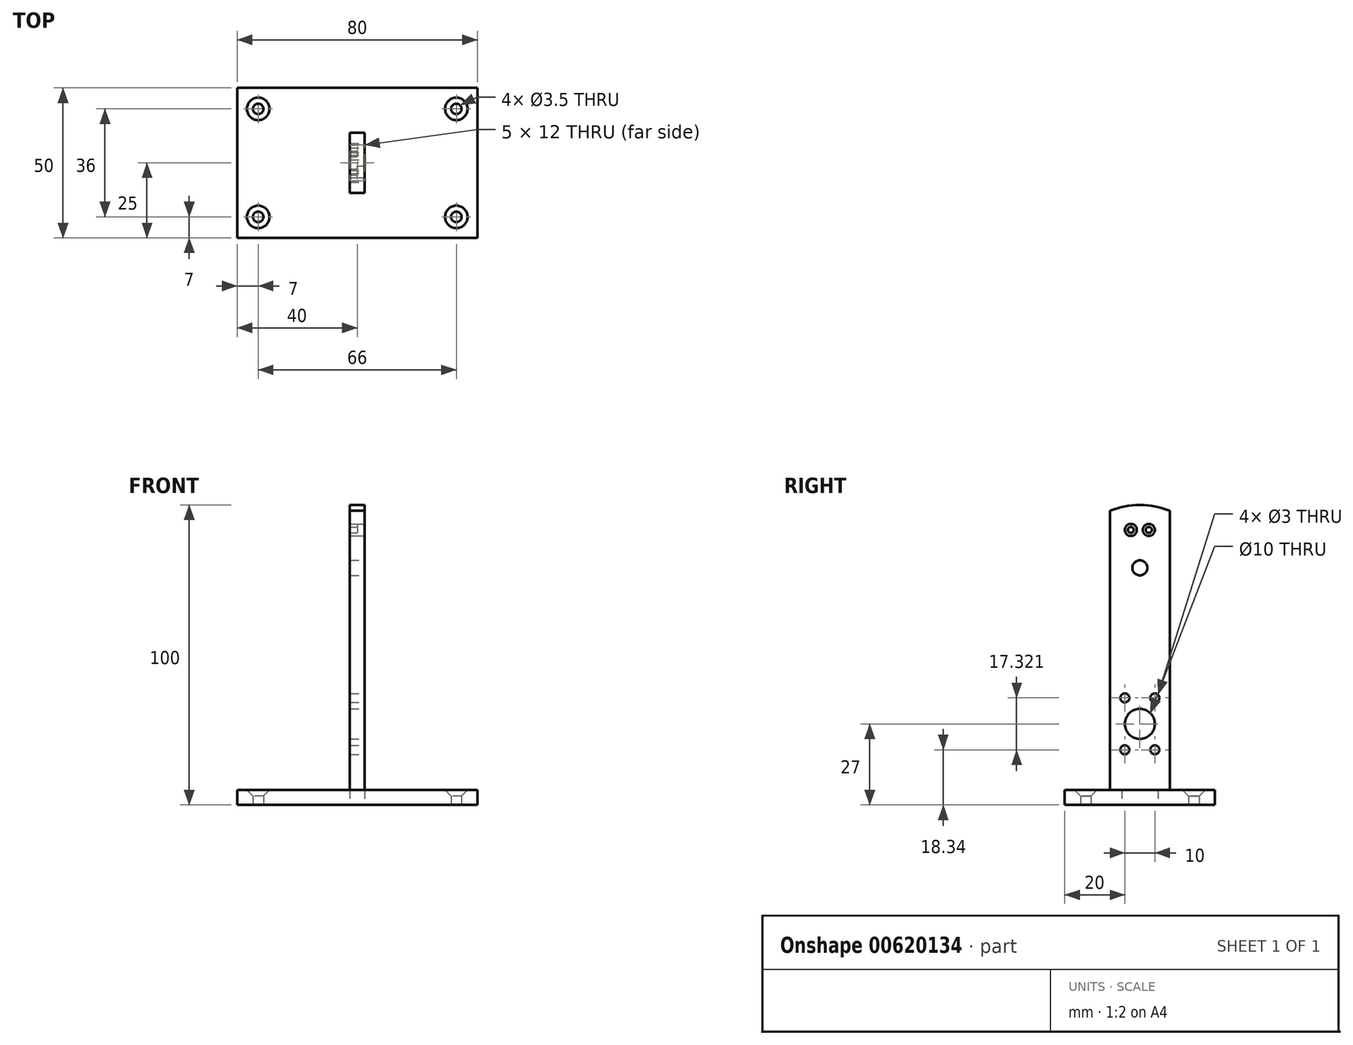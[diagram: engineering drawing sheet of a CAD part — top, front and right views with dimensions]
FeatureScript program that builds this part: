
annotation { "Feature Type Name" : "Feature", "Feature Type Description" : "" }
export const myFeature = defineFeature(function(context is Context, id is Id, definition is map)
    precondition{}
    {
        {
            var Q0;
            Q0=qCreatedBy(makeId("Top.planeOp"),FACE);
            var sketch = newSketch(context, id + "F0", { "sketchPlane" : qUnion([Q0])});
            skLineSegment(sketch, "E0.bottom", {"start": v(0, 0) * mm, "end": v(80, 0) * mm});
            skLineSegment(sketch, "E0.top", {"start": v(0, 50) * mm, "end": v(80, 50) * mm});
            skLineSegment(sketch, "E0.left", {"start": v(0, 0) * mm, "end": v(0, 50) * mm});
            skLineSegment(sketch, "E0.right", {"start": v(80, 0) * mm, "end": v(80, 50) * mm});
            skLineSegment(sketch, "E1.bottom", {"start": v(37.5, 31) * mm, "end": v(42.5, 31) * mm});
            skLineSegment(sketch, "E1.top", {"start": v(37.5, 19) * mm, "end": v(42.5, 19) * mm});
            skLineSegment(sketch, "E1.left", {"start": v(37.5, 31) * mm, "end": v(37.5, 19) * mm});
            skLineSegment(sketch, "E1.right", {"start": v(42.5, 31) * mm, "end": v(42.5, 19) * mm});
            skCircle(sketch, "E2", {"center": v(7, 7) * mm, "radius": 1.75 * mm});
            skLineSegment(sketch, "E3", {"start": v(40, 50) * mm, "end": v(40, 0) * mm, "construction": true});
            skLineSegment(sketch, "E4", {"start": v(0, 25) * mm, "end": v(80, 25) * mm, "construction": true});
            skCircle(sketch, "E5.MirrorC", {"center": v(73, 7) * mm, "radius": 1.75 * mm});
            skCircle(sketch, "E6.MirrorC", {"center": v(7, 43) * mm, "radius": 1.75 * mm});
            skCircle(sketch, "E7.MirrorC", {"center": v(73, 43) * mm, "radius": 1.75 * mm});
            skSolve(sketch);
        }
        {
            var Q0;
            Q0=makeQuery(id+"F0.imprint","IMPRINT",FACE,{"disambiguationData":[TD([[makeQuery(id+"F0.imprint","IMPRINT",EDGE,{"derivedFrom":sQuery(id+"F0.wireOp",EDGE,"E0.bottom")}),1.0]])]});
            extrude(context, id + "F1", {"entities" : qUnion([Q0]), "depth" : 5 * mm, "offsetDistance" : 25 * mm});
        }
        {
            var Q0;
            Q0=makeQuery(id+"F1.opExtrude","CAP_EDGE",EDGE,{"disambiguationData":[OSD([sQuery(id+"F0.wireOp",EDGE,"E6.MirrorC")])],"isStart":false});
            var Q1;
            Q1=makeQuery(id+"F1.opExtrude","CAP_EDGE",EDGE,{"disambiguationData":[OSD([sQuery(id+"F0.wireOp",EDGE,"E7.MirrorC")])],"isStart":false});
            var Q2;
            Q2=makeQuery(id+"F1.opExtrude","CAP_EDGE",EDGE,{"disambiguationData":[OSD([sQuery(id+"F0.wireOp",EDGE,"E5.MirrorC")])],"isStart":false});
            var Q3;
            Q3=makeQuery(id+"F1.opExtrude","CAP_EDGE",EDGE,{"disambiguationData":[OSD([sQuery(id+"F0.wireOp",EDGE,"E2")])],"isStart":false});
            chamfer(context, id + "F2", {"entities" : qUnion([Q0, Q1, Q2, Q3]), "width" : 2 * mm, "tangentPropagation" : true});
        }
        {
            var Q0;
            Q0=makeQuery(id+"F1.opExtrude","SWEPT_FACE",FACE,{"disambiguationData":[OSD([sQuery(id+"F0.wireOp",EDGE,"E1.right")])]});
            var sketch = newSketch(context, id + "F3", { "sketchPlane" : qUnion([Q0])});
            skLineSegment(sketch, "E8.0", {"start": v(-31, 0) * mm, "end": v(-19, 0) * mm});
            skLineSegment(sketch, "E9.0", {"start": v(-31, 5) * mm, "end": v(-31, 0) * mm});
            skLineSegment(sketch, "E10.0", {"start": v(-19, 5) * mm, "end": v(-19, 0) * mm});
            skLineSegment(sketch, "E11", {"start": v(-31, 5) * mm, "end": v(-35, 5) * mm});
            skLineSegment(sketch, "E12", {"start": v(-19, 5) * mm, "end": v(-15, 5) * mm});
            skLineSegment(sketch, "E13", {"start": v(-35, 5) * mm, "end": v(-35, 100) * mm});
            skLineSegment(sketch, "E14", {"start": v(-15, 5) * mm, "end": v(-15, 100) * mm});
            skLineSegment(sketch, "E15", {"start": v(-35, 100) * mm, "end": v(-15, 100) * mm});
            skLineSegment(sketch, "E16", {"start": v(-25, 100) * mm, "end": v(-25, 0) * mm, "construction": true});
            skCircle(sketch, "E17", {"center": v(-25, 27) * mm, "radius": 5 * mm});
            skCircle(sketch, "E18", {"center": v(-25, 27) * mm, "radius": 10 * mm, "construction": true});
            skCircle(sketch, "E19", {"center": v(-30, 35.66) * mm, "radius": 1.5 * mm});
            skLineSegment(sketch, "E20", {"start": v(-15, 27) * mm, "end": v(-35, 27) * mm, "construction": true});
            skCircle(sketch, "E21.MirrorC", {"center": v(-20, 35.66) * mm, "radius": 1.5 * mm});
            skCircle(sketch, "E22.MirrorC", {"center": v(-30, 18.34) * mm, "radius": 1.5 * mm});
            skCircle(sketch, "E23.MirrorC", {"center": v(-20, 18.34) * mm, "radius": 1.5 * mm});
            skCircle(sketch, "E24", {"center": v(-25, 79) * mm, "radius": 2.5 * mm});
            skArc(sketch, "E25", {"start": v(-15, 87.3) * mm, "mid": v(-25, 92) * mm, "end": v(-35, 87.3) * mm, "construction": true});
            skCircle(sketch, "E26", {"center": v(-22, 91.65) * mm, "radius": 1 * mm});
            skCircle(sketch, "E27.MirrorC", {"center": v(-28, 91.65) * mm, "radius": 1 * mm});
            skArc(sketch, "E28", {"start": v(-15, 98) * mm, "mid": v(-25, 100) * mm, "end": v(-35, 98) * mm});
            skCircle(sketch, "E29", {"center": v(-22, 91.65) * mm, "radius": 2 * mm});
            skCircle(sketch, "E30", {"center": v(-28, 91.65) * mm, "radius": 2 * mm});
            skSolve(sketch);
        }
        {
            var Q0;
            {var subQ0=sQuery(id+"F3.wireOp",EDGE,"E11");Q0=makeQuery(id+"F3.imprint","IMPRINT",FACE,{"disambiguationData":[TD([[makeQuery(id+"F3.imprint","IMPRINT",EDGE,{"derivedFrom":subQ0}),-1.0]])]});}
            var Q1;
            Q1=makeQuery(id+"F3.imprint","IMPRINT",FACE,{"disambiguationData":[TD([[makeQuery(id+"F3.imprint","IMPRINT",EDGE,{"derivedFrom":sQuery(id+"F3.wireOp",EDGE,"E8.0")}),1.0]])]});
            var Q2;
            Q2=makeQuery(id+"F3.imprint","IMPRINT",FACE,{"disambiguationData":[TD([[makeQuery(id+"F3.imprint","IMPRINT",EDGE,{"derivedFrom":sQuery(id+"F3.wireOp",EDGE,"E26")}),-1.0]])]});
            var Q3;
            Q3=makeQuery(id+"F3.imprint","IMPRINT",FACE,{"disambiguationData":[TD([[makeQuery(id+"F3.imprint","IMPRINT",EDGE,{"derivedFrom":sQuery(id+"F3.wireOp",EDGE,"E27.MirrorC")}),1.0]])]});
            extrude(context, id + "F4", {"entities" : qUnion([Q0, Q1, Q2, Q3]), "depth" : 5 * mm, "offsetDistance" : 25 * mm});
        }
        {
            var Q0;
            Q0=makeQuery(id+"F3.imprint","IMPRINT",FACE,{"disambiguationData":[TD([[makeQuery(id+"F3.imprint","IMPRINT",EDGE,{"derivedFrom":sQuery(id+"F3.wireOp",EDGE,"E26")}),-1.0]])]});
            var Q1;
            Q1=makeQuery(id+"F3.imprint","IMPRINT",FACE,{"disambiguationData":[TD([[makeQuery(id+"F3.imprint","IMPRINT",EDGE,{"derivedFrom":sQuery(id+"F3.wireOp",EDGE,"E27.MirrorC")}),1.0]])]});
            extrude(context, id + "F5", {"entities" : qUnion([Q0, Q1]), "operationType" : NewBodyOperationType.REMOVE, "depth" : 2.5 * mm, "offsetDistance" : 25 * mm});
        }
    });
